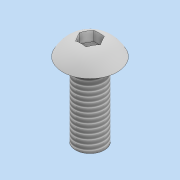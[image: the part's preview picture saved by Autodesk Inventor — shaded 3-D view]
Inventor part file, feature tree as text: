
AUTODESK INVENTOR PART (.ipt)
format: ipt  version: 2022 (Build 260153000, 153)  size: 119,808 bytes
history: native  units: in
note: dims shown in document units (in); Inventor stores cm internally (conversion verified against a paired STEP export)
features: sketch x3, extrude x2, revolve x1, thread x1, plane x1
ambient origin geometry x8: Origin, YZ Plane, XZ Plane, XY Plane, X Axis, Y Axis, Z Axis, Center Point
bodies: Solid1 (feature_tree)
feature tree (8):
  revolve  "Revolution1"  [1 undecoded]
  extrude  "Extrusion1"  Depth=0.1969in
  thread  "Thread1"  [1 undecoded]
  plane  "Work Plane1"
  extrude  "Extrusion2"  [1 undecoded]
  sketch  "Sketch1"  dims[d0=0.185in d1=0.1181in]
  sketch  "Sketch2"  dims[d2=90.0deg d3=0.1969in d4=0.5039in d5=0.0in]
  sketch  "Sketch3"  dims[d6=0.5039in d7=0.0in d8=-0.1181in d9=0.062in d10=0.0787in d11=0.0in]
note: 3 required parameter values undecoded (feature->parameter linkage not recoverable at this tier; creation-order binding heuristic only, values carry confidence <= 0.55)